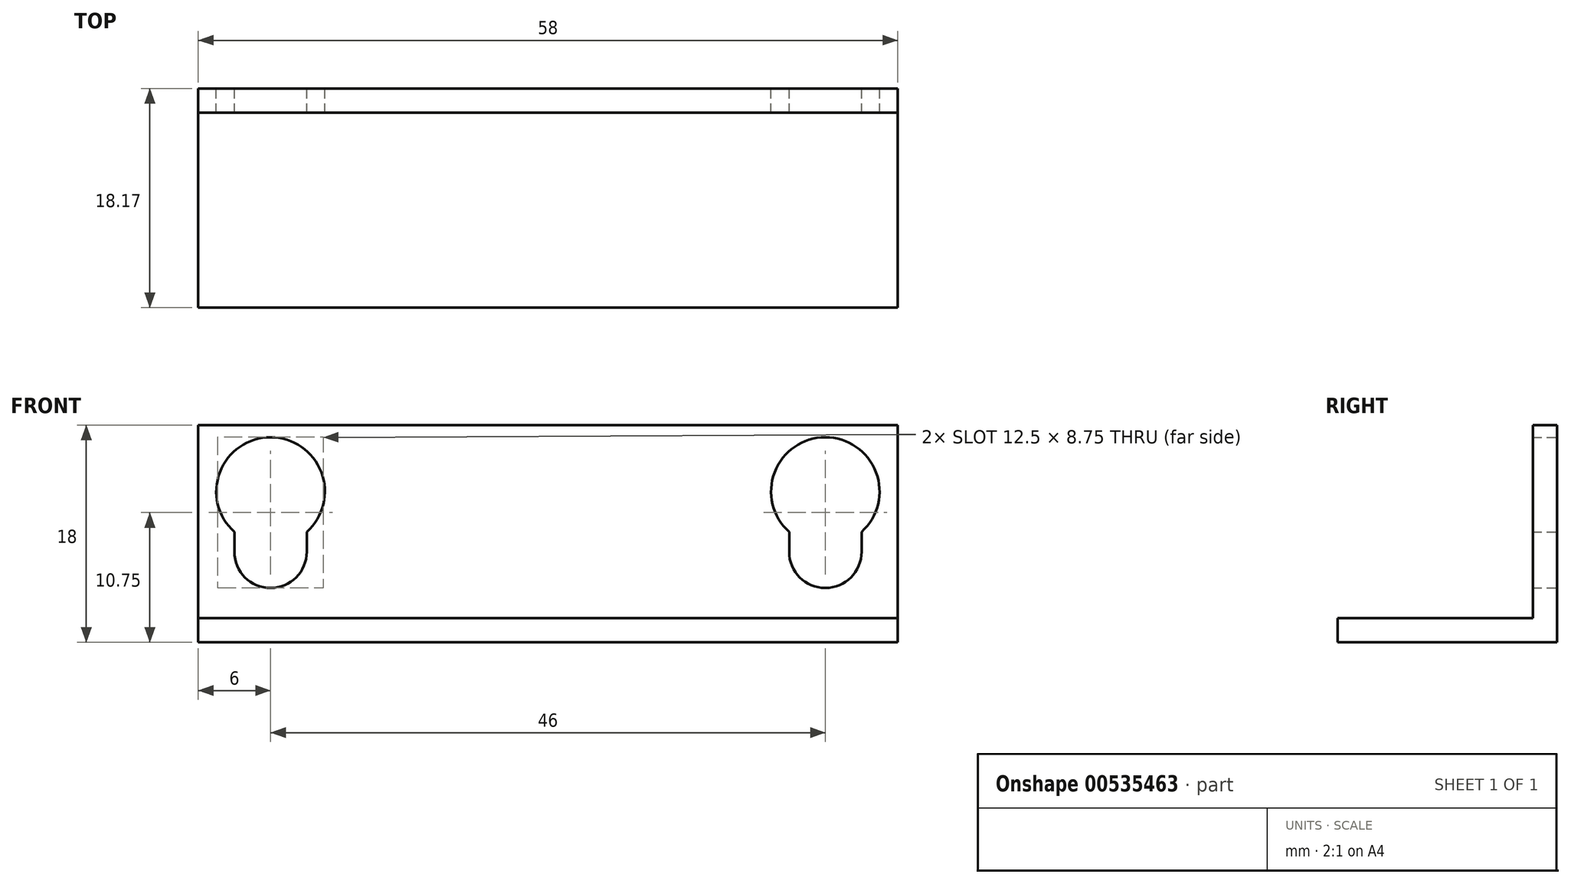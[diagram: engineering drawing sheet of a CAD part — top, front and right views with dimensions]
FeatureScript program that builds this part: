
annotation { "Feature Type Name" : "Feature", "Feature Type Description" : "" }
export const myFeature = defineFeature(function(context is Context, id is Id, definition is map)
    precondition{}
    {
        {
            var Q0;
            Q0=qCreatedBy(makeId("Front.planeOp"),FACE);
            var sketch = newSketch(context, id + "F0", { "sketchPlane" : qUnion([Q0])});
            skLineSegment(sketch, "E0.bottom", {"start": v(-29, 16) * mm, "end": v(29, 16) * mm});
            skLineSegment(sketch, "E0.top", {"start": v(-29, 0) * mm, "end": v(29, 0) * mm});
            skLineSegment(sketch, "E0.left", {"start": v(-29, 16) * mm, "end": v(-29, 0) * mm});
            skLineSegment(sketch, "E0.right", {"start": v(29, 16) * mm, "end": v(29, 0) * mm});
            skArc(sketch, "E1", {"start": v(20, 5.5) * mm, "mid": v(23, 2.5) * mm, "end": v(26, 5.5) * mm});
            skArc(sketch, "E2", {"start": v(-26, 5.5) * mm, "mid": v(-23, 2.5) * mm, "end": v(-20, 5.5) * mm});
            skArc(sketch, "E3", {"start": v(26, 7.15) * mm, "mid": v(23, 15) * mm, "end": v(20, 7.15) * mm});
            skArc(sketch, "E4", {"start": v(-20, 7.15) * mm, "mid": v(-23, 15) * mm, "end": v(-26, 7.15) * mm});
            skLineSegment(sketch, "E5", {"start": v(0, 0) * mm, "end": v(0, 35.78) * mm, "construction": true});
            skLineSegment(sketch, "E6", {"start": v(26, 5.5) * mm, "end": v(26, 7.15) * mm});
            skLineSegment(sketch, "E7", {"start": v(20, 5.5) * mm, "end": v(20, 7.15) * mm});
            skLineSegment(sketch, "E8", {"start": v(-20, 5.5) * mm, "end": v(-20, 7.15) * mm});
            skLineSegment(sketch, "E9", {"start": v(-26, 5.5) * mm, "end": v(-26, 7.15) * mm});
            skSolve(sketch);
        }
        {
            var Q0;
            Q0=makeQuery(id+"F0.imprint","IMPRINT",FACE,{"disambiguationData":[TD([[makeQuery(id+"F0.imprint","IMPRINT",EDGE,{"derivedFrom":sQuery(id+"F0.wireOp",EDGE,"E0.bottom")}),-1.0]])]});
            extrude(context, id + "F1", {"entities" : qUnion([Q0]), "depth" : 2 * mm, "offsetDistance" : 25 * mm});
        }
        {
            var Q0;
            Q0=qCreatedBy(makeId("Top.planeOp"),FACE);
            var sketch = newSketch(context, id + "F2", { "sketchPlane" : qUnion([Q0])});
            skLineSegment(sketch, "E10.bottom", {"start": v(-29, -2) * mm, "end": v(29, -2) * mm});
            skLineSegment(sketch, "E10.top", {"start": v(-29, -18.17) * mm, "end": v(29, -18.17) * mm});
            skLineSegment(sketch, "E10.left", {"start": v(-29, -2) * mm, "end": v(-29, -18.17) * mm});
            skLineSegment(sketch, "E10.right", {"start": v(29, -2) * mm, "end": v(29, -18.17) * mm});
            skSolve(sketch);
        }
        {
            var Q0;
            Q0=makeQuery(id+"F2.imprint","IMPRINT",FACE,{"disambiguationData":[TD([[makeQuery(id+"F2.imprint","IMPRINT",EDGE,{"derivedFrom":sQuery(id+"F2.wireOp",EDGE,"E10.bottom")}),-1.0]])]});
            var Q1;
            Q1=makeQuery(id+"F1.opExtrude","SWEPT_FACE",FACE,{"disambiguationData":[OSD([sQuery(id+"F0.wireOp",EDGE,"E0.top")])]});
            extrude(context, id + "F3", {"entities" : qUnion([Q0, Q1]), "operationType" : NewBodyOperationType.ADD, "oppositeDirection" : true, "depth" : 2 * mm, "offsetDistance" : 25 * mm});
        }
    });
